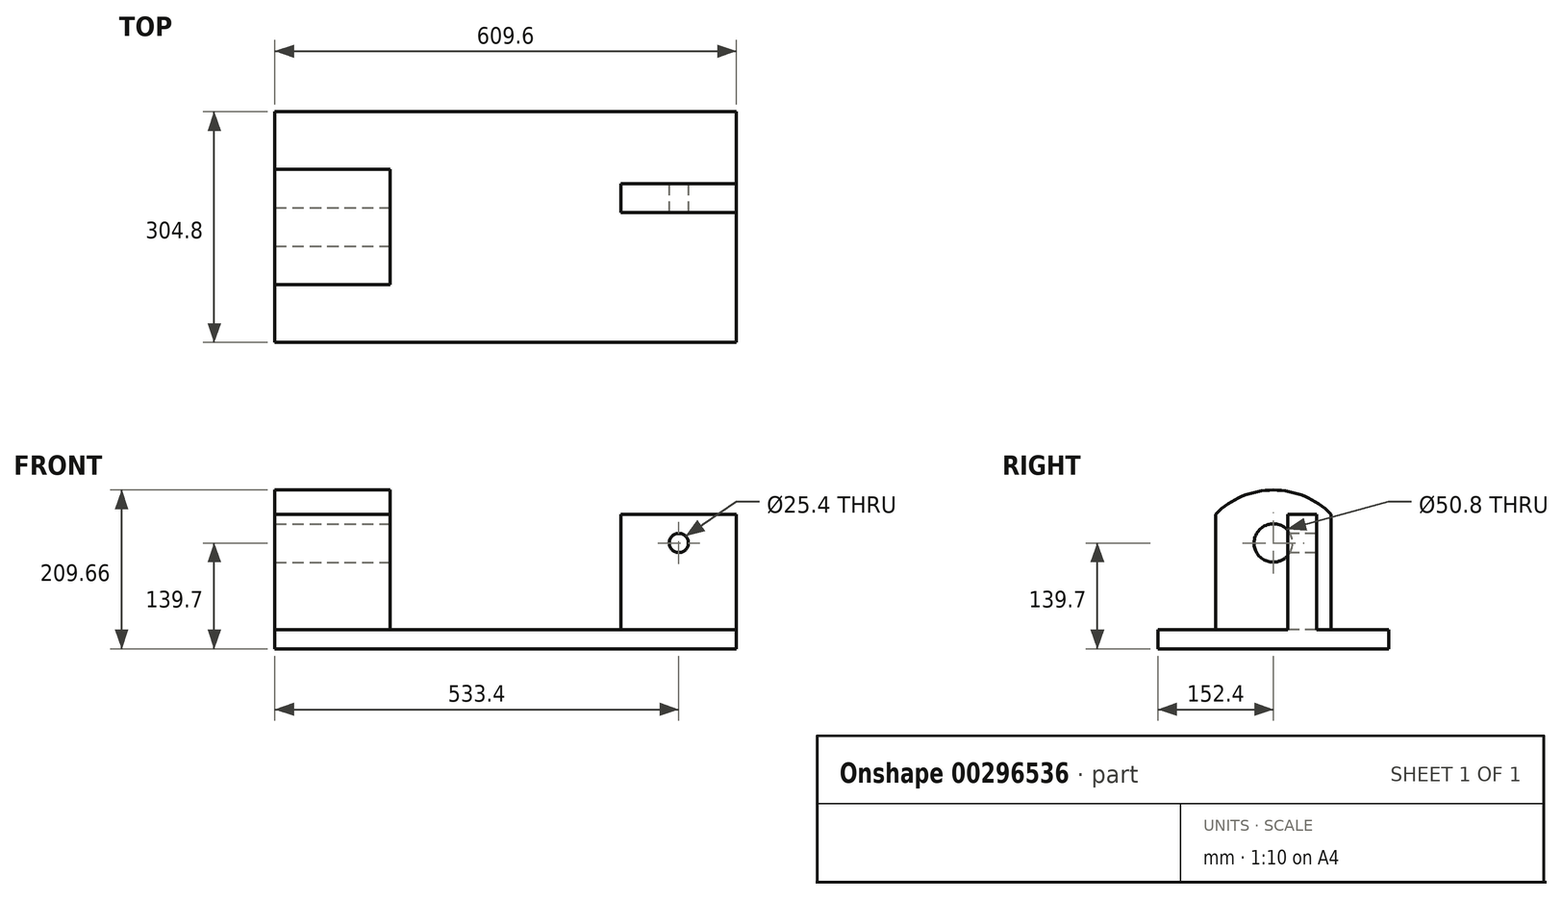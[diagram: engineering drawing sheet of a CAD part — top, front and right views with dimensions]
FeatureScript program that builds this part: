
annotation { "Feature Type Name" : "Feature", "Feature Type Description" : "" }
export const myFeature = defineFeature(function(context is Context, id is Id, definition is map)
    precondition{}
    {
        {
            var Q0;
            Q0=qCreatedBy(makeId("Top.planeOp"),FACE);
            var sketch = newSketch(context, id + "F0", { "sketchPlane" : qUnion([Q0])});
            skLineSegment(sketch, "E0.bottom", {"start": v(-304.8, 152.4) * mm, "end": v(304.8, 152.4) * mm});
            skLineSegment(sketch, "E0.top", {"start": v(-304.8, -152.4) * mm, "end": v(304.8, -152.4) * mm});
            skLineSegment(sketch, "E0.left", {"start": v(-304.8, 152.4) * mm, "end": v(-304.8, -152.4) * mm});
            skLineSegment(sketch, "E0.right", {"start": v(304.8, 152.4) * mm, "end": v(304.8, -152.4) * mm});
            skLineSegment(sketch, "E1", {"start": v(-304.8, 0) * mm, "end": v(-304.8, 152.4) * mm});
            skSolve(sketch);
        }
        {
            var Q0;
            Q0=makeQuery(id+"F0.imprint","IMPRINT",FACE,{"disambiguationData":[TD([[makeQuery(id+"F0.imprint","IMPRINT",EDGE,{"derivedFrom":sQuery(id+"F0.wireOp",EDGE,"E0.bottom")}),-1.0]])]});
            extrude(context, id + "F1", {"entities" : qUnion([Q0]), "oppositeDirection" : true, "depth" : 25.4 * mm});
        }
        {
            var Q0;
            Q0=makeQuery(id+"F1.opExtrude","CAP_FACE",FACE,{"disambiguationData":[OSD([sQuery(id+"F0.wireOp",EDGE,"E0.bottom"),sQuery(id+"F0.wireOp",EDGE,"E0.top"),sQuery(id+"F0.wireOp",EDGE,"E0.left"),sQuery(id+"F0.wireOp",EDGE,"E0.right"),sQuery(id+"F0.wireOp",EDGE,"E1")])],"isStart":true});
            var sketch = newSketch(context, id + "F2", { "sketchPlane" : qUnion([Q0])});
            skLineSegment(sketch, "E2.bottom", {"start": v(-304.8, 76.2) * mm, "end": v(-152.4, 76.2) * mm});
            skLineSegment(sketch, "E2.top", {"start": v(-304.8, -76.2) * mm, "end": v(-152.4, -76.2) * mm});
            skLineSegment(sketch, "E2.left", {"start": v(-304.8, 76.2) * mm, "end": v(-304.8, -76.2) * mm});
            skLineSegment(sketch, "E2.right", {"start": v(-152.4, 76.2) * mm, "end": v(-152.4, -76.2) * mm});
            skSolve(sketch);
        }
        {
            var Q0;
            Q0=makeQuery(id+"F2.imprint","IMPRINT",FACE,{"disambiguationData":[TD([[makeQuery(id+"F2.imprint","IMPRINT",EDGE,{"derivedFrom":sQuery(id+"F2.wireOp",EDGE,"E2.bottom")}),-1.0]])]});
            extrude(context, id + "F3", {"entities" : qUnion([Q0]), "operationType" : NewBodyOperationType.ADD, "depth" : 152.4 * mm});
        }
        {
            var Q0;
            Q0=makeQuery(id+"F3.opExtrude","SWEPT_FACE",FACE,{"disambiguationData":[OSD([sQuery(id+"F2.wireOp",EDGE,"E2.right")])]});
            var sketch = newSketch(context, id + "F4", { "sketchPlane" : qUnion([Q0])});
            skCircle(sketch, "E3", {"center": v(0, 114.3) * mm, "radius": 25.4 * mm});
            skSolve(sketch);
        }
        {
            var Q0;
            Q0=makeQuery(id+"F4.imprint","IMPRINT",FACE,{"disambiguationData":[TD([[makeQuery(id+"F4.imprint","IMPRINT",EDGE,{"derivedFrom":sQuery(id+"F4.wireOp",EDGE,"E3")}),1.0]])]});
            extrude(context, id + "F5", {"entities" : qUnion([Q0]), "operationType" : NewBodyOperationType.REMOVE, "endBound" : BoundingType.THROUGH_ALL, "oppositeDirection" : true, "depth" : 25.4 * mm});
        }
        {
            var Q0;
            Q0=makeQuery(id+"F1.opExtrude","CAP_FACE",FACE,{"disambiguationData":[OSD([sQuery(id+"F0.wireOp",EDGE,"E0.bottom"),sQuery(id+"F0.wireOp",EDGE,"E0.top"),sQuery(id+"F0.wireOp",EDGE,"E0.left"),sQuery(id+"F0.wireOp",EDGE,"E0.right"),sQuery(id+"F0.wireOp",EDGE,"E1")])],"isStart":true});
            var sketch = newSketch(context, id + "F6", { "sketchPlane" : qUnion([Q0])});
            skLineSegment(sketch, "E4", {"start": v(-152.4, 0) * mm, "end": v(304.8, 0) * mm, "construction": true});
            skLineSegment(sketch, "E5.bottom", {"start": v(304.8, 57.15) * mm, "end": v(152.4, 57.15) * mm});
            skLineSegment(sketch, "E5.top", {"start": v(304.8, 19.05) * mm, "end": v(152.4, 19.05) * mm});
            skLineSegment(sketch, "E5.left", {"start": v(304.8, 57.15) * mm, "end": v(304.8, 19.05) * mm});
            skLineSegment(sketch, "E5.right", {"start": v(152.4, 57.15) * mm, "end": v(152.4, 19.05) * mm});
            skSolve(sketch);
        }
        {
            var Q0;
            Q0=makeQuery(id+"F6.imprint","IMPRINT",FACE,{"disambiguationData":[TD([[makeQuery(id+"F6.imprint","IMPRINT",EDGE,{"derivedFrom":sQuery(id+"F6.wireOp",EDGE,"E5.bottom")}),1.0]])]});
            extrude(context, id + "F7", {"entities" : qUnion([Q0]), "operationType" : NewBodyOperationType.ADD, "depth" : 152.4 * mm});
        }
        {
            var Q0;
            Q0=makeQuery(id+"F7.opExtrude","SWEPT_FACE",FACE,{"disambiguationData":[OSD([sQuery(id+"F6.wireOp",EDGE,"E5.top")])]});
            var sketch = newSketch(context, id + "F8", { "sketchPlane" : qUnion([Q0])});
            skCircle(sketch, "E6", {"center": v(228.6, 114.3) * mm, "radius": 12.7 * mm});
            skPoint(sketch, "E6.centerSnap0", {"position": v(228.6, 152.4) * mm});
            skSolve(sketch);
        }
        {
            var Q0;
            Q0=makeQuery(id+"F8.imprint","IMPRINT",FACE,{"disambiguationData":[TD([[makeQuery(id+"F8.imprint","IMPRINT",EDGE,{"derivedFrom":sQuery(id+"F8.wireOp",EDGE,"E6")}),1.0]])]});
            extrude(context, id + "F9", {"entities" : qUnion([Q0]), "operationType" : NewBodyOperationType.REMOVE, "endBound" : BoundingType.THROUGH_ALL, "oppositeDirection" : true, "depth" : 25.4 * mm});
        }
        {
            var Q0;
            Q0=makeQuery(id+"F3.opExtrude","SWEPT_FACE",FACE,{"disambiguationData":[OSD([sQuery(id+"F2.wireOp",EDGE,"E2.right")])]});
            var sketch = newSketch(context, id + "F10", { "sketchPlane" : qUnion([Q0])});
            skArc(sketch, "E7", {"start": v(76.2, 152.4) * mm, "mid": v(0, 184.26) * mm, "end": v(-76.2, 152.4) * mm});
            skLineSegment(sketch, "E8", {"start": v(-76.2, 152.4) * mm, "end": v(76.2, 152.4) * mm});
            skSolve(sketch);
        }
        {
            var Q0;
            Q0=makeQuery(id+"F10.imprint","IMPRINT",FACE,{"disambiguationData":[TD([[makeQuery(id+"F10.imprint","IMPRINT",EDGE,{"derivedFrom":sQuery(id+"F10.wireOp",EDGE,"E7")}),1.0]])]});
            var Q1;
            Q1=makeQuery(id+"F3.boolean.opBoolean","MERGE",FACE,{"derivedFrom":[makeQuery(id+"F1.opExtrude","SWEPT_FACE",FACE,{"disambiguationData":[OSD([sQuery(id+"F0.wireOp",EDGE,"E0.left"),sQuery(id+"F0.wireOp",EDGE,"E1")])]}),makeQuery(id+"F3.opExtrude","SWEPT_FACE",FACE,{"disambiguationData":[OSD([sQuery(id+"F2.wireOp",EDGE,"E2.left")])]})]});
            extrude(context, id + "F11", {"entities" : qUnion([Q0]), "operationType" : NewBodyOperationType.ADD, "endBound" : BoundingType.UP_TO_SURFACE, "oppositeDirection" : true, "endBoundEntityFace" : qUnion([Q1]), "depth" : 25.4 * mm});
        }
    });
